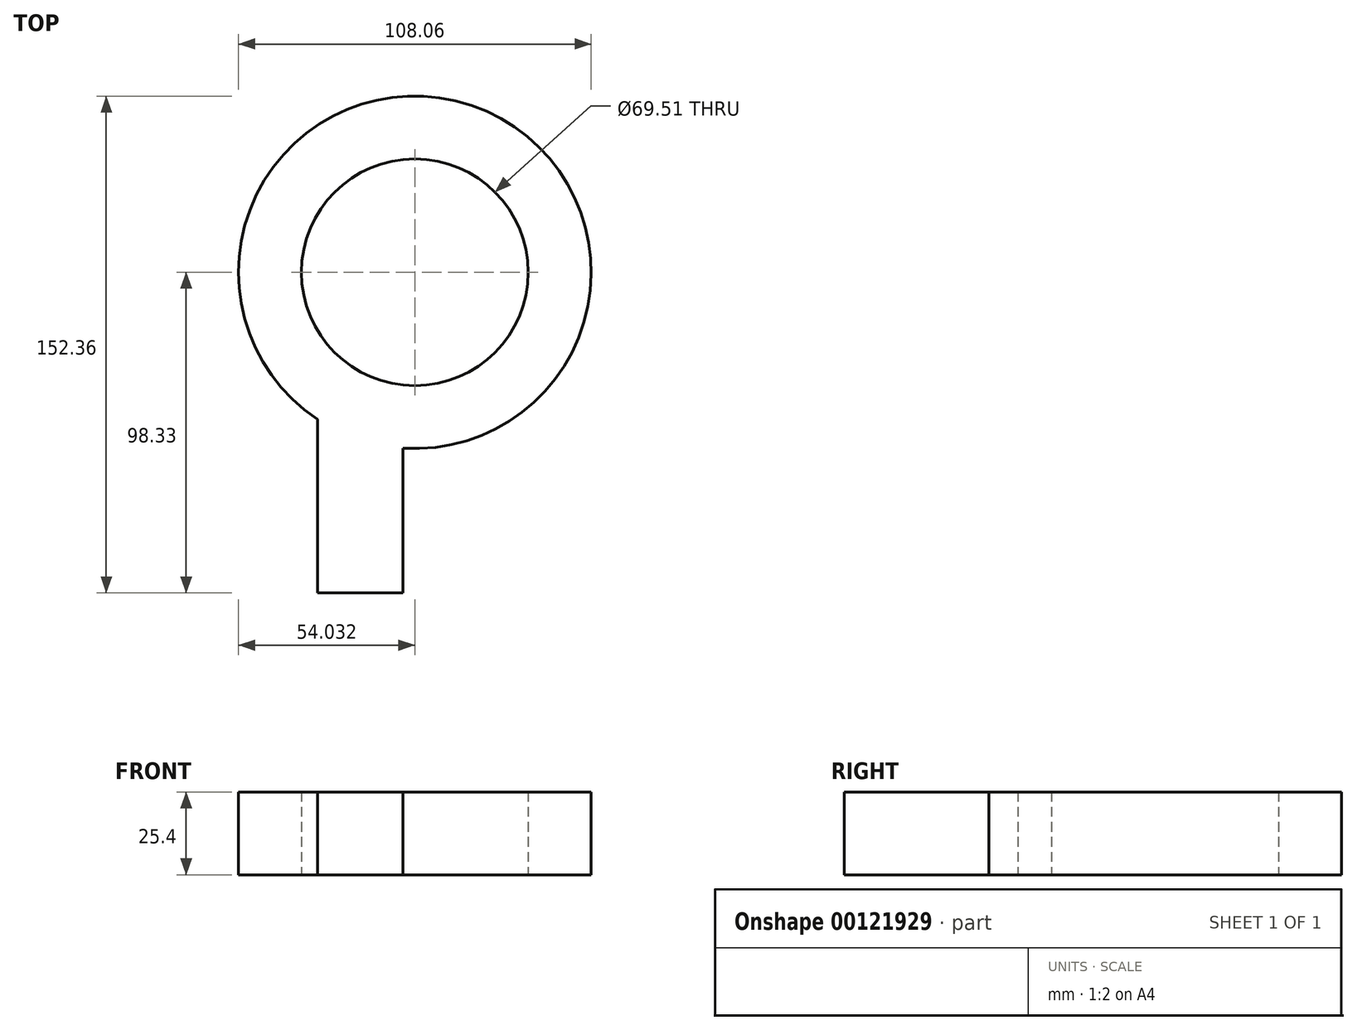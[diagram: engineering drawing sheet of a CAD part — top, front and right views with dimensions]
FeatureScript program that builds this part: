
annotation { "Feature Type Name" : "Feature", "Feature Type Description" : "" }
export const myFeature = defineFeature(function(context is Context, id is Id, definition is map)
    precondition{}
    {
        {
            var Q0;
            Q0=qCreatedBy(makeId("Top.planeOp"),FACE);
            var sketch = newSketch(context, id + "F0", { "sketchPlane" : qUnion([Q0])});
            skCircle(sketch, "E0", {"center": v(-141.46, 0) * mm, "radius": 54.03 * mm});
            skCircle(sketch, "E1", {"center": v(-141.46, 0) * mm, "radius": 34.75 * mm});
            skSolve(sketch);
        }
        {
            var Q0;
            Q0=makeQuery(id+"F0.imprint","IMPRINT",FACE,{"disambiguationData":[TD([[makeQuery(id+"F0.imprint","IMPRINT",EDGE,{"derivedFrom":sQuery(id+"F0.wireOp",EDGE,"E0")}),1.0]])]});
            extrude(context, id + "F1", {"entities" : qUnion([Q0]), "depth" : 25.4 * mm});
        }
        {
            var Q0;
            Q0=qCreatedBy(makeId("Top.planeOp"),FACE);
            var sketch = newSketch(context, id + "F2", { "sketchPlane" : qUnion([Q0])});
            skLineSegment(sketch, "E2.bottom", {"start": v(-171.24, -44.43) * mm, "end": v(-145.08, -44.43) * mm});
            skLineSegment(sketch, "E2.top", {"start": v(-171.24, -98.33) * mm, "end": v(-145.08, -98.33) * mm});
            skLineSegment(sketch, "E2.left", {"start": v(-171.24, -44.43) * mm, "end": v(-171.24, -98.33) * mm});
            skLineSegment(sketch, "E2.right", {"start": v(-145.08, -44.43) * mm, "end": v(-145.08, -98.33) * mm});
            skSolve(sketch);
        }
        {
            var Q0;
            Q0 = qSketchRegion(id + "F2", true);
            extrude(context, id + "F3", {"entities" : qUnion([Q0]), "operationType" : NewBodyOperationType.ADD, "depth" : 25.4 * mm});
        }
    });
